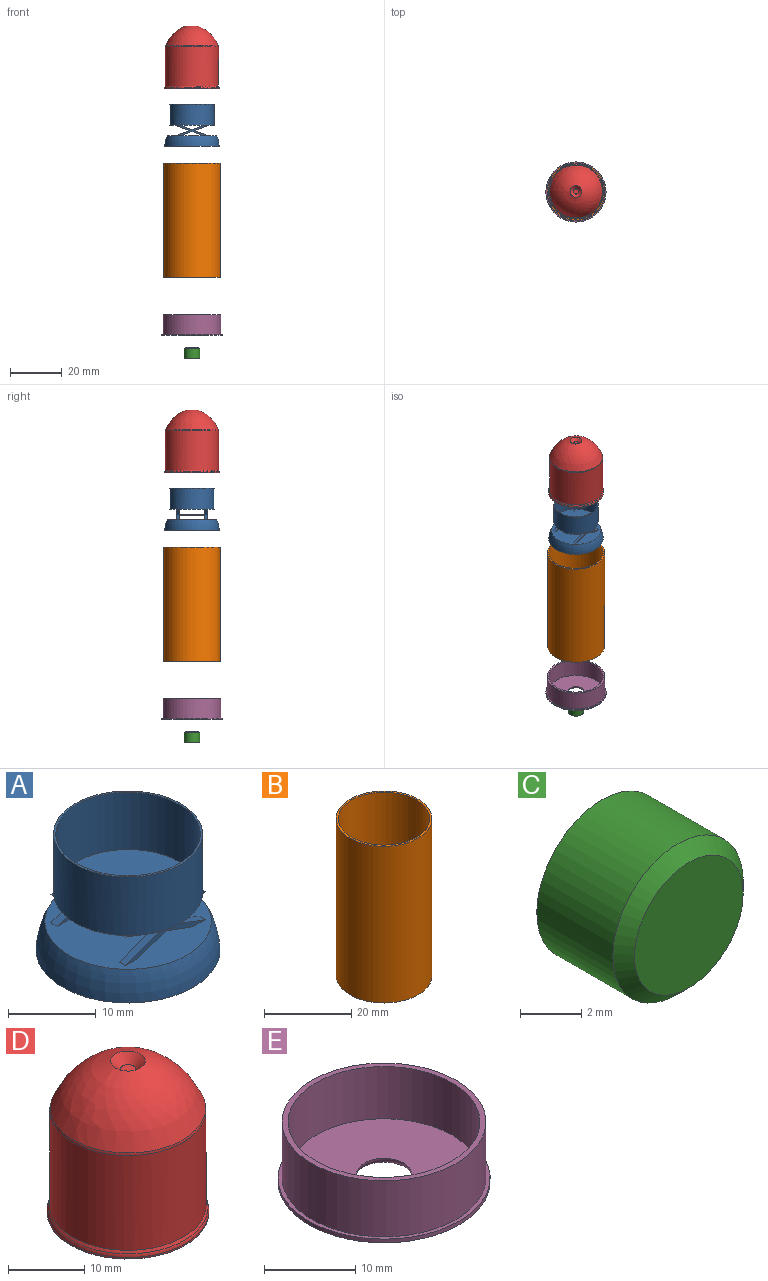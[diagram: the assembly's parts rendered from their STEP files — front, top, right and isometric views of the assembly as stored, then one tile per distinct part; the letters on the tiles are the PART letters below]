
ASSEMBLY  parts=5 mates=4
PART A: 40 faces, bbox 21x21x16.2 mm
  f0: plane 17.01x17.01mm, normal (0,0,-1), area 219.3mm2, adj f1,f6,f7,f8,f9,f10,f11,f12
  f1: cylinder r=8.5mm len=17mm, axis (0,0,1), area 437.9mm2, adj f0,f2,f3,f4,f5,f37
  f2: plane 0.45x0.43mm, normal (0,0,1), area 0.1mm2, adj f1,f8,f21
  f3: plane 0.45x0.43mm, normal (0,0,1), area 0.1mm2, adj f1,f8,f18
  f4: plane 0.46x0.43mm, normal (0,0,1), area 0.1mm2, adj f1,f12,f25
  f5: plane 0.45x0.43mm, normal (0,0,1), area 0.1mm2, adj f1,f12,f26
  f6: plane 4.43x1.63mm, normal (0.34,0,0.94), area 4.7mm2, adj f0,f7,f8,f9
  f7: plane 4.43x1.63mm, normal (-0.34,0,0.94), area 4.7mm2, adj f0,f6,f8,f9
  f8: plane 12.89x4mm, normal (0,1,0), area 15.2mm2, adj f0,f2,f3,f6,f7,f14,f17,f18
  f9: plane 12.9x4mm, normal (0,-1,0), area 14.8mm2, adj f0,f6,f7,f14,f17,f18,f19,f20
  f10: plane 4.43x1.63mm, normal (-0.34,0,0.94), area 4.7mm2, adj f0,f11,f12,f13
  f11: plane 4.43x1.63mm, normal (0.34,0,0.94), area 4.7mm2, adj f0,f10,f12,f13
  f12: plane 12.89x4mm, normal (0,-1,0), area 15.2mm2, adj f0,f4,f5,f10,f11,f14,f25,f26
  f13: plane 12.89x4mm, normal (0,1,0), area 14.8mm2, adj f0,f10,f11,f14,f25,f26,f27,f28
  f14: plane 19x18.95mm, normal (0,0,1), area 275.5mm2, adj f8,f9,f12,f13,f16,f17,f19,f20
  f15: plane 21x21mm, normal (0,0,-1), area 77.5mm2, adj f16,f23,f24,f35
  f16: torus R=0.21mm, axis (0,0,1), area 264.3mm2, adj f14,f15,f24
  f17: plane 5.45x2mm, normal (-0.34,0,0.94), area 5.8mm2, adj f8,f9,f14,f18
  f18: plane 5.46x2.01mm, normal (-0.34,0,-0.94), area 5.8mm2, adj f0,f3,f8,f9,f17
  f19: plane 4.45x1.63mm, normal (-0.34,0,-0.94), area 4.7mm2, adj f8,f9,f14,f20
  f20: plane 4.45x1.63mm, normal (0.34,0,-0.94), area 4.7mm2, adj f8,f9,f14,f19
  f21: plane 5.45x2mm, normal (0.34,0,-0.94), area 5.8mm2, adj f0,f2,f8,f9,f22
  f22: plane 5.45x2mm, normal (0.34,0,0.94), area 5.8mm2, adj f8,f9,f14,f21
  f23: plane 4x2mm, normal (1,0,0), area 8mm2, adj f14,f15,f24
  f24: cylinder r=9.5mm len=4mm, axis (0,0,1), area 8mm2, adj f15,f16,f23
  f25: plane 5.46x2.01mm, normal (0.34,0,-0.94), area 5.8mm2, adj f0,f4,f12,f13,f30
  f26: plane 5.45x2mm, normal (-0.34,0,-0.94), area 5.8mm2, adj f0,f5,f12,f13,f27
  f27: plane 5.45x2mm, normal (-0.34,0,0.94), area 5.8mm2, adj f12,f13,f14,f26
  f28: plane 4.45x1.63mm, normal (0.34,0,-0.94), area 4.7mm2, adj f12,f13,f14,f29
  f29: plane 4.45x1.63mm, normal (-0.34,0,-0.94), area 4.7mm2, adj f12,f13,f14,f28
  f30: plane 5.45x2mm, normal (0.34,0,0.94), area 5.8mm2, adj f12,f13,f14,f25
  f31: plane 10x1.01mm, normal (0,0,-1), area 10.1mm2, adj f9,f13,f32,f34
  f32: plane 10x0.45mm, normal (1,0,0), area 4.5mm2, adj f9,f13,f31,f33
  f33: plane 10x1.01mm, normal (0,0,1), area 10.1mm2, adj f9,f13,f32,f34
  f34: plane 10x0.45mm, normal (-1,0,0), area 4.5mm2, adj f9,f13,f31,f33
  f35: cylinder r=9.25mm len=18.5mm, axis (0,0,-1), area 116.2mm2, adj f15,f36
  f36: plane 18.5x18.5mm, normal (0,0,-1), area 268.8mm2, adj f35
  f37: plane 17x17mm, normal (0,0,1), area 13.2mm2, adj f1,f38
  f38: cylinder r=8.25mm len=16.5mm, axis (0,0,1), area 414.7mm2, adj f37,f39
  f39: plane 16.5x16.5mm, normal (0,0,1), area 213.8mm2, adj f38
PART B: 4 faces, bbox 22x22x44 mm
  f0: cylinder r=11mm len=44mm, axis (0,0,-1), area 3041.1mm2, adj f1,f2
  f1: plane 22x22mm, normal (0,0,1), area 33.8mm2, adj f0,f3
  f2: plane 22x22mm, normal (0,0,-1), area 33.8mm2, adj f0,f3
  f3: cylinder r=10.5mm len=44mm, axis (0,0,1), area 2902.8mm2, adj f1,f2
PART C: 4 faces, bbox 6x4x6 mm
  f0: cylinder r=3mm len=6mm, axis (0,1,0), area 66mm2, adj f2,f3
  f1: plane 5x5mm, normal (0,-1,0), area 19.6mm2, adj f2
  f2: cone r=2.5mm half-angle=45deg, axis (0,1,0), area 12.2mm2, adj f0,f1
  f3: plane 6x6mm, normal (0,1,0), area 28.3mm2, adj f0
PART D: 9 faces, bbox 22.9x22.9x24.3 mm
  f0: plane 21.2x21.2mm, normal (0,0,-1), area 353mm2, adj f1
  f1: cylinder r=10.6mm len=21.2mm, axis (0,0,-1), area 15.5mm2, adj f0,f5
  f2: cone r=10.6mm half-angle=30deg, axis (0,0,-1), area 30.2mm2, adj f3,f5
  f3: cylinder r=10.23mm len=20.47mm, axis (0,0,-1), area 978.3mm2, adj f2,f6
  f4: revolved ~20.34x20.34mm, area 481.3mm2, adj f6,f8
  f5: torus R=9.6mm, axis (0,0,1), area 34.7mm2, adj f1,f2
  f6: torus R=9.23mm, axis (0,0,1), area 23.5mm2, adj f3,f4
  f7: plane 2x2mm, normal (0,0,1), area 3.1mm2, adj f8
  f8: cone r=3mm half-angle=45deg, axis (0,0,1), area 18.4mm2, adj f4,f7
PART E: 8 faces, bbox 23.2x23.2x8 mm
  f0: plane 23.2x23.2mm, normal (0,0,-1), area 372.5mm2, adj f1,f6
  f1: cylinder r=11.6mm len=23.2mm, axis (0,0,1), area 36.4mm2, adj f0,f2
  f2: plane 23.2x23.2mm, normal (0,0,1), area 32.2mm2, adj f1,f3
  f3: cylinder r=11.15mm len=22.3mm, axis (0,0,1), area 525.4mm2, adj f2,f7
  f4: cylinder r=10.5mm len=21mm, axis (0,0,1), area 461.8mm2, adj f5,f7
  f5: plane 21x21mm, normal (0,0,1), area 318.1mm2, adj f4,f6
  f6: torus R=4mm, axis (0,0,1), area 33.2mm2, adj f0,f5
  f7: plane 22.3x22.3mm, normal (0,0,1), area 44.2mm2, adj f3,f4
PLACE A t=(-39.69,109.65,49.17)mm
PLACE B rot(axis=(1,0,0),180deg) t=(-39.69,109.65,38.58)mm
PLACE C rot(axis=(-1,0,0),90deg) t=(-39.69,109.65,-33.51)mm
PLACE D t=(-39.69,109.65,77.33)mm
PLACE E t=(-39.69,109.65,-8.51)mm
MATE cylindrical D.f1 <-> A.f38  axis (0,0,-1) through (-39.69,109.65,67.23)mm
MATE cylindrical B.f3 <-> E.f4  axis (0,0,-1) through (-39.69,109.65,-5.42)mm
MATE cylindrical A.f35 <-> E.f4  axis (0,0,-1) through (-39.69,109.65,45.17)mm
MATE cylindrical C.f0 <-> E.f6  axis (0,0,-1) through (-39.69,109.65,-36.51)mm
